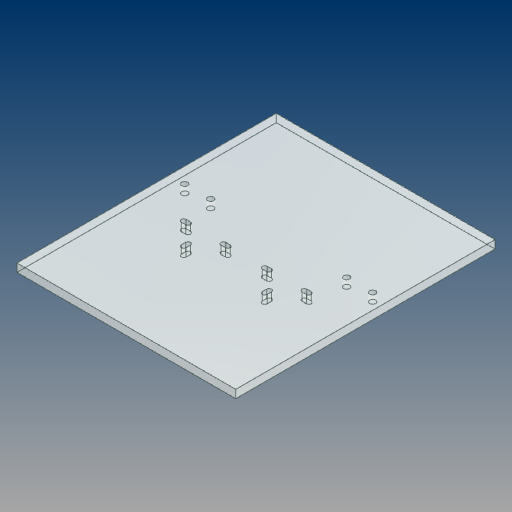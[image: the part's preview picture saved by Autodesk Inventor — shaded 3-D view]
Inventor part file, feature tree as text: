
AUTODESK INVENTOR PART (.ipt)
format: ipt  version: 2021 (Build 250183000, 183)  size: 155,136 bytes
history: native  units: mm
features: other x10, reference x8, extrude x2, sketch x2
ambient origin geometry x8: Origin, YZ Plane, XZ Plane, XY Plane, X Axis, Y Axis, Z Axis, Center Point
bodies: Solid1 (feature_tree)
feature tree (22):
  extrude  "Extrusion1"  Depth=320.0mm
  extrude  "Extrusion2"  Depth=10.0mm TaperAngle=0.0deg
  sketch  "Sketch1"  dims[d0=270.0mm d1=320.0mm]
  sketch  "Sketch2"  dims[d2=10.0mm d3=0.0mm d4=10.0mm d5=0.0mm]
  reference  "Reference1"
  reference  "Reference2"
  reference  "Reference3"
  reference  "Reference4"
  reference  "Reference5"
  reference  "Reference6"
  reference  "Reference7"
  reference  "Reference8"
  other  "0002_ASS_Ban_lap_ghep_02.iam"
  other  "0002_Tam_nguyen_Truc_Z:1"
  other  "ke-nhom-noi-2020:4"
  other  "ke-nhom-noi-2020:5"
  other  "ke-nhom-noi-2020:3"
  other  "ke-nhom-noi-2020:6"
  other  "ke-nhom-noi-2020:2"
  other  "ke-nhom-noi-2020:1"
  other  "SHF8:2"
  other  "SHF8:1"
